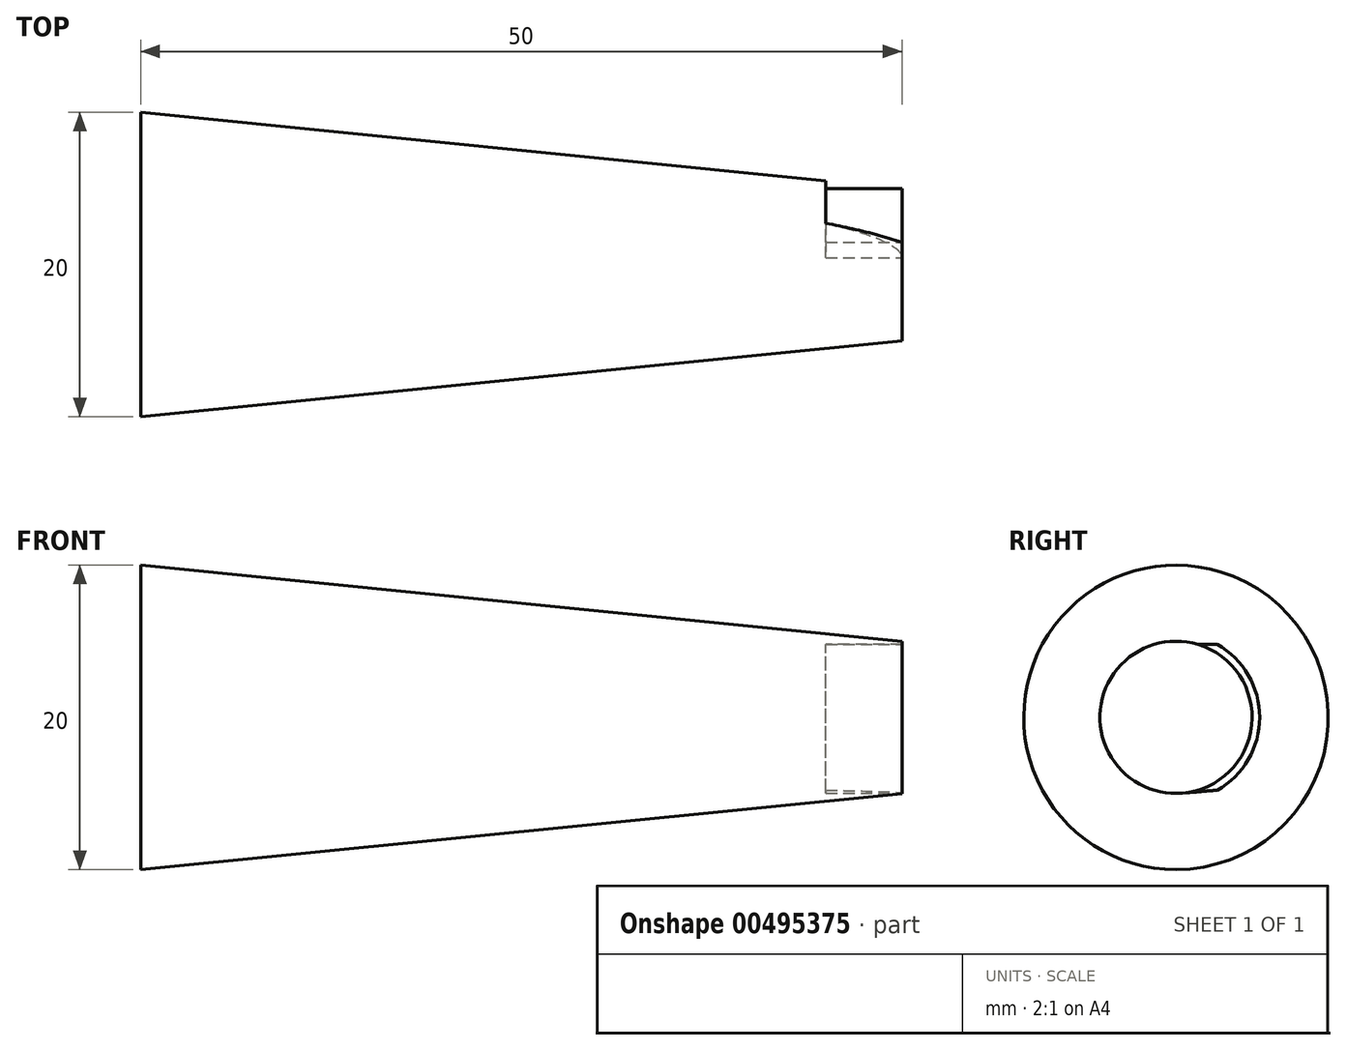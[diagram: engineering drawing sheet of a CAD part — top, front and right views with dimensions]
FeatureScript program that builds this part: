
annotation { "Feature Type Name" : "Feature", "Feature Type Description" : "" }
export const myFeature = defineFeature(function(context is Context, id is Id, definition is map)
    precondition{}
    {
        {
            var Q0;
            Q0=qCreatedBy(makeId("Right.planeOp"),FACE);
            cPlane(context, id + "F0", {"entities" : qUnion([Q0]), "cplaneType" : CPlaneType.OFFSET, "offset" : 50 * mm, "width" : 150 * mm, "height" : 150 * mm});
        }
        {
            var Q0;
            Q0=qCreatedBy(id+"F0.planeOp",FACE);
            var sketch = newSketch(context, id + "F1", { "sketchPlane" : qUnion([Q0])});
            skCircle(sketch, "E0", {"center": v(0, 0) * mm, "radius": 5 * mm});
            skSolve(sketch);
        }
        {
            var Q0;
            Q0=qCreatedBy(makeId("Right.planeOp"),FACE);
            var sketch = newSketch(context, id + "F2", { "sketchPlane" : qUnion([Q0])});
            skCircle(sketch, "E1", {"center": v(0, 0) * mm, "radius": 10 * mm});
            skSolve(sketch);
        }
        {
            var Q0;
            Q0=makeQuery(id+"F1.imprint","IMPRINT",FACE,{"disambiguationData":[TD([[makeQuery(id+"F1.imprint","IMPRINT",EDGE,{"derivedFrom":sQuery(id+"F1.wireOp",EDGE,"E0")}),1.0]])]});
            var Q1;
            Q1=makeQuery(id+"F2.imprint","IMPRINT",FACE,{"disambiguationData":[TD([[makeQuery(id+"F2.imprint","IMPRINT",EDGE,{"derivedFrom":sQuery(id+"F2.wireOp",EDGE,"E1")}),1.0]])]});
            loft(context, id + "F3", {"sheetProfilesArray" : [{ "sheetProfileEntities" : qUnion([Q0]) }, { "sheetProfileEntities" : qUnion([Q1]) }]});
        }
        {
            var Q0;
            Q0=makeQuery(id+"F3.opLoft","CAP_FACE",FACE,{"disambiguationData":[OSD([makeQuery(id+"F1.imprint","IMPRINT",FACE,{"disambiguationData":[TD([[makeQuery(id+"F1.imprint","IMPRINT",EDGE,{"derivedFrom":sQuery(id+"F1.wireOp",EDGE,"E0")}),1.0]])]})])],"isStart":true});
            var sketch = newSketch(context, id + "F4", { "sketchPlane" : qUnion([Q0])});
            skLineSegment(sketch, "E2.bottom", {"start": v(-3.1, 3.92) * mm, "end": v(-2.74, 3.92) * mm});
            skLineSegment(sketch, "E2.top", {"start": v(-3.1, -3.99) * mm, "end": v(-2.64, -3.99) * mm});
            skLineSegment(sketch, "E2.left", {"start": v(-3.1, 3.92) * mm, "end": v(-3.1, 3.64) * mm});
            skCircle(sketch, "E3", {"center": v(0, 0) * mm, "radius": 4.78 * mm});
            skLineSegment(sketch, "E4.trimOffspring", {"start": v(-3.1, -3.64) * mm, "end": v(-3.1, -3.99) * mm});
            skLineSegment(sketch, "E5", {"start": v(0, 4.78) * mm, "end": v(5.65, 4.78) * mm});
            skLineSegment(sketch, "E6", {"start": v(5.65, 4.78) * mm, "end": v(5.65, 3.92) * mm});
            skLineSegment(sketch, "E7", {"start": v(5.65, 3.92) * mm, "end": v(5.65, -4.53) * mm});
            skLineSegment(sketch, "E8", {"start": v(5.65, -4.53) * mm, "end": v(0, -5.02) * mm});
            skLineSegment(sketch, "E9", {"start": v(0, -5.02) * mm, "end": v(0, 4.78) * mm});
            skSolve(sketch);
        }
        {
            var Q0;
            {var subQ4=sQuery(id+"F4.wireOp",EDGE,"E6");Q0=makeQuery(id+"F4.imprint","IMPRINT",FACE,{"disambiguationData":[TD([[makeQuery(id+"F4.imprint","IMPRINT",EDGE,{"derivedFrom":subQ4}),-1.0]])]});}
            extrude(context, id + "F5", {"entities" : qUnion([Q0]), "operationType" : NewBodyOperationType.REMOVE, "oppositeDirection" : true, "depth" : 5 * mm});
        }
    });
